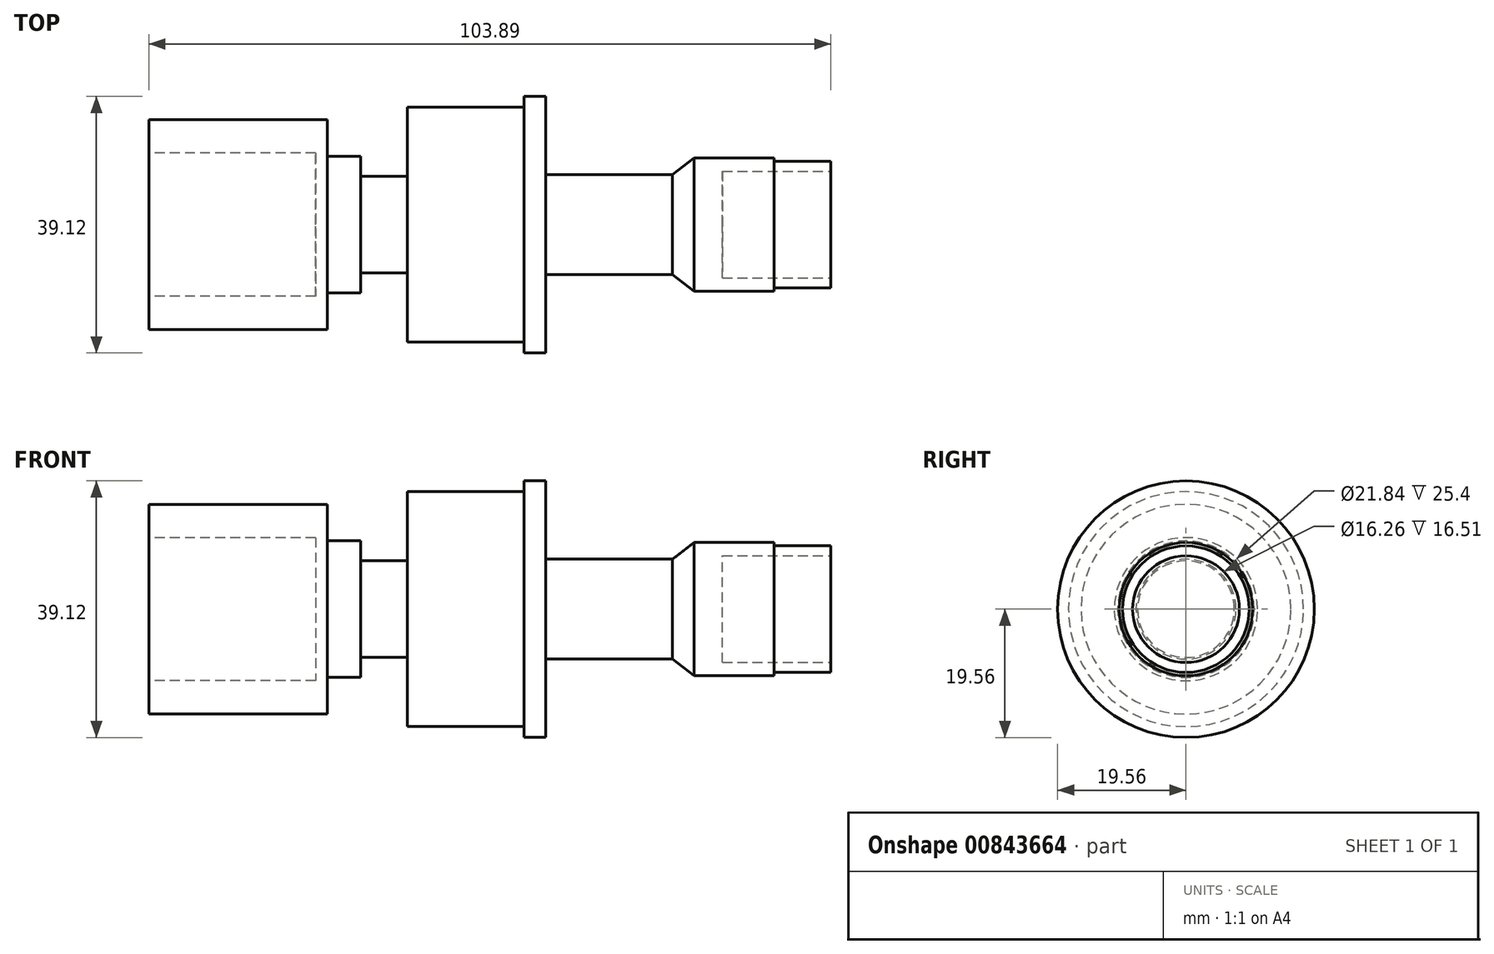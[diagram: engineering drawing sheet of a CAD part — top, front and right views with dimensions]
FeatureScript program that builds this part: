
annotation { "Feature Type Name" : "Feature", "Feature Type Description" : "" }
export const myFeature = defineFeature(function(context is Context, id is Id, definition is map)
    precondition{}
    {
        {
            var Q0;
            Q0=qCreatedBy(makeId("Front.planeOp"),FACE);
            var sketch = newSketch(context, id + "F0", { "sketchPlane" : qUnion([Q0])});
            skLineSegment(sketch, "E0", {"start": v(-38.4, 0) * mm, "end": v(20.4, 0) * mm});
            skLineSegment(sketch, "E1.bottom", {"start": v(-11.22, 16) * mm, "end": v(-38.4, 16) * mm});
            skLineSegment(sketch, "E1.right", {"start": v(-38.4, 16) * mm, "end": v(-38.4, 0) * mm});
            skPoint(sketch, "E1.middle", {"position": v(-24.8, 0) * mm});
            skLineSegment(sketch, "E2.bottom", {"start": v(-11.22, 10.41) * mm, "end": v(-6.14, 10.41) * mm});
            skLineSegment(sketch, "E2.left", {"start": v(-11.22, 10.41) * mm, "end": v(-11.22, 0) * mm});
            skPoint(sketch, "E2.middle", {"position": v(-8.68, 0) * mm});
            skLineSegment(sketch, "E3.bottom", {"start": v(-6.14, 7.37) * mm, "end": v(0.97, 7.37) * mm});
            skLineSegment(sketch, "E3.left", {"start": v(-6.14, 7.37) * mm, "end": v(-6.14, 0) * mm});
            skPoint(sketch, "E3.middle", {"position": v(-2.58, 0) * mm});
            skLineSegment(sketch, "E4.bottom", {"start": v(0.97, 17.9) * mm, "end": v(18.75, 17.9) * mm});
            skPoint(sketch, "E4.middle", {"position": v(9.86, 0) * mm});
            skLineSegment(sketch, "E5.bottom", {"start": v(18.75, 19.56) * mm, "end": v(22.05, 19.56) * mm});
            skLineSegment(sketch, "E5.top", {"start": v(18.75, -19.56) * mm, "end": v(22.05, -19.56) * mm});
            skPoint(sketch, "E5.middle", {"position": v(20.4, 0) * mm});
            skPoint(sketch, "E6.middle", {"position": v(41.25, 0) * mm});
            skLineSegment(sketch, "E7.bottom", {"start": v(44.66, 10.16) * mm, "end": v(56.85, 10.16) * mm});
            skPoint(sketch, "E7.middle", {"position": v(50.76, 0) * mm});
            skLineSegment(sketch, "E8.bottom", {"start": v(56.85, 9.65) * mm, "end": v(65.49, 9.65) * mm});
            skPoint(sketch, "E8.middle", {"position": v(61.17, 0) * mm});
            skLineSegment(sketch, "E9.bottom", {"start": v(41.36, 7.62) * mm, "end": v(22.05, 7.62) * mm});
            skPoint(sketch, "E9.middle", {"position": v(30.82, 0) * mm});
            skLineSegment(sketch, "E10.trimOffspring", {"start": v(22.05, 0) * mm, "end": v(65.49, 0) * mm});
            skLineSegment(sketch, "E11.right", {"start": v(41.34, 7.62) * mm, "end": v(41.34, 0) * mm});
            skPoint(sketch, "E11.middle", {"position": v(43, 0) * mm});
            skLineSegment(sketch, "E12", {"start": v(41.36, 7.62) * mm, "end": v(44.66, 10.16) * mm});
            skPoint(sketch, "E13", {"position": v(-38.4, 0) * mm});
            skLineSegment(sketch, "E14", {"start": v(-11.22, 16) * mm, "end": v(-11.22, 10.41) * mm});
            skLineSegment(sketch, "E15", {"start": v(-6.14, 10.41) * mm, "end": v(-6.14, 7.37) * mm});
            skLineSegment(sketch, "E16", {"start": v(0.97, 7.37) * mm, "end": v(0.97, 0) * mm});
            skLineSegment(sketch, "E17", {"start": v(0.97, 0) * mm, "end": v(0.97, 7.37) * mm});
            skLineSegment(sketch, "E18", {"start": v(0.97, 17.9) * mm, "end": v(0.97, 7.37) * mm});
            skLineSegment(sketch, "E19", {"start": v(18.75, 19.56) * mm, "end": v(18.75, 0) * mm});
            skLineSegment(sketch, "E20", {"start": v(22.72, 0) * mm, "end": v(20.4, 0) * mm});
            skLineSegment(sketch, "E21", {"start": v(22.05, 7.62) * mm, "end": v(22.05, 0) * mm});
            skLineSegment(sketch, "E22", {"start": v(22.05, 19.56) * mm, "end": v(22.05, 7.62) * mm});
            skLineSegment(sketch, "E23", {"start": v(44.66, 10.16) * mm, "end": v(44.66, 0) * mm});
            skLineSegment(sketch, "E24", {"start": v(56.85, 10.16) * mm, "end": v(56.85, 0) * mm});
            skLineSegment(sketch, "E25", {"start": v(65.49, 9.65) * mm, "end": v(65.49, 0) * mm});
            skSolve(sketch);
        }
        {
            var Q0;
            Q0=makeQuery(id+"F0.imprint","IMPRINT",FACE,{"disambiguationData":[TD([[makeQuery(id+"F0.imprint","IMPRINT",EDGE,{"derivedFrom":sQuery(id+"F0.wireOp",EDGE,"E1.bottom")}),1.0]])]});
            var Q1;
            Q1=sQuery(id+"F0.wireOp",EDGE,"E0");
            revolve(context, id + "F1", {"surfaceOperationType" : NewSurfaceOperationType.NEW, "entities" : qUnion([Q0]), "axis" : qUnion([Q1]), "revolveType" : RevolveType.FULL});
        }
        {
            var Q0;
            Q0=makeQuery(id+"F0.imprint","IMPRINT",FACE,{"disambiguationData":[TD([[makeQuery(id+"F0.imprint","IMPRINT",EDGE,{"derivedFrom":sQuery(id+"F0.wireOp",EDGE,"E2.bottom")}),-1.0]])]});
            var Q1;
            Q1=sQuery(id+"F0.wireOp",EDGE,"E0");
            revolve(context, id + "F2", {"operationType" : NewBodyOperationType.ADD, "surfaceOperationType" : NewSurfaceOperationType.NEW, "entities" : qUnion([Q0]), "axis" : qUnion([Q1]), "revolveType" : RevolveType.FULL});
        }
        {
            var Q0;
            {var subQ1=sQuery(id+"F0.wireOp",EDGE,"E4.bottom");Q0=makeQuery(id+"F0.imprint","IMPRINT",FACE,{"disambiguationData":[TD([[makeQuery(id+"F0.imprint","IMPRINT",EDGE,{"derivedFrom":subQ1}),-1.0]])]});}
            var Q1;
            {var subQ4=sQuery(id+"F0.wireOp",EDGE,"E5.bottom");Q1=makeQuery(id+"F0.imprint","IMPRINT",FACE,{"disambiguationData":[TD([[makeQuery(id+"F0.imprint","IMPRINT",EDGE,{"derivedFrom":subQ4}),-1.0]])]});}
            var Q2;
            Q2=makeQuery(id+"F0.imprint","IMPRINT",FACE,{"disambiguationData":[TD([[makeQuery(id+"F0.imprint","IMPRINT",EDGE,{"derivedFrom":sQuery(id+"F0.wireOp",EDGE,"E3.bottom")}),-1.0]])]});
            var Q3;
            {var subQ3=sQuery(id+"F0.wireOp",EDGE,"E11.right");Q3=makeQuery(id+"F0.imprint","IMPRINT",FACE,{"disambiguationData":[TD([[makeQuery(id+"F0.imprint","IMPRINT",EDGE,{"derivedFrom":subQ3}),-1.0]])]});}
            var Q4;
            {var subQ1=sQuery(id+"F0.wireOp",EDGE,"E11.right");Q4=makeQuery(id+"F0.imprint","IMPRINT",FACE,{"disambiguationData":[TD([[makeQuery(id+"F0.imprint","IMPRINT",EDGE,{"derivedFrom":subQ1}),1.0]])]});}
            var Q5;
            {var subQ5=sQuery(id+"F0.wireOp",EDGE,"E7.bottom");Q5=makeQuery(id+"F0.imprint","IMPRINT",FACE,{"disambiguationData":[TD([[makeQuery(id+"F0.imprint","IMPRINT",EDGE,{"derivedFrom":subQ5}),-1.0]])]});}
            var Q6;
            {var subQ0=sQuery(id+"F0.wireOp",EDGE,"E8.bottom");Q6=makeQuery(id+"F0.imprint","IMPRINT",FACE,{"disambiguationData":[TD([[makeQuery(id+"F0.imprint","IMPRINT",EDGE,{"derivedFrom":subQ0}),-1.0]])]});}
            var Q7;
            Q7=sQuery(id+"F0.wireOp",EDGE,"E0");
            revolve(context, id + "F3", {"operationType" : NewBodyOperationType.ADD, "surfaceOperationType" : NewSurfaceOperationType.NEW, "entities" : qUnion([Q0, Q1, Q2, Q3, Q4, Q5, Q6]), "axis" : qUnion([Q7]), "revolveType" : RevolveType.FULL});
        }
        {
            var Q0;
            Q0=makeQuery(id+"F1.opRevolve","SWEPT_FACE",FACE,{"disambiguationData":[OSD([sQuery(id+"F0.wireOp",EDGE,"E1.right")])]});
            var sketch = newSketch(context, id + "F4", { "sketchPlane" : qUnion([Q0])});
            skCircle(sketch, "E26", {"center": v(0, 0) * mm, "radius": 10.92 * mm});
            skCircle(sketch, "E27.0", {"center": v(0, 0) * mm, "radius": 16 * mm});
            skSolve(sketch);
        }
        {
            var Q0;
            Q0=makeQuery(id+"F4.imprint","IMPRINT",FACE,{"disambiguationData":[TD([[makeQuery(id+"F4.imprint","IMPRINT",EDGE,{"derivedFrom":sQuery(id+"F4.wireOp",EDGE,"E26")}),1.0]])]});
            extrude(context, id + "F5", {"entities" : qUnion([Q0]), "operationType" : NewBodyOperationType.REMOVE, "oppositeDirection" : true, "depth" : 25.4 * mm, "offsetDistance" : 25.4 * mm});
        }
        {
            var Q0;
            Q0=makeQuery(id+"F3.opRevolve","SWEPT_FACE",FACE,{"disambiguationData":[OSD([sQuery(id+"F0.wireOp",EDGE,"E25")])]});
            var sketch = newSketch(context, id + "F6", { "sketchPlane" : qUnion([Q0])});
            skCircle(sketch, "E28", {"center": v(0, 0) * mm, "radius": 8.13 * mm});
            skCircle(sketch, "E29.0", {"center": v(0, 0) * mm, "radius": 9.65 * mm});
            skSolve(sketch);
        }
        {
            var Q0;
            Q0=makeQuery(id+"F6.imprint","IMPRINT",FACE,{"disambiguationData":[TD([[makeQuery(id+"F6.imprint","IMPRINT",EDGE,{"derivedFrom":sQuery(id+"F6.wireOp",EDGE,"E28")}),1.0]])]});
            extrude(context, id + "F7", {"entities" : qUnion([Q0]), "operationType" : NewBodyOperationType.REMOVE, "oppositeDirection" : true, "depth" : 16.5 * mm, "offsetDistance" : 25.4 * mm});
        }
    });
